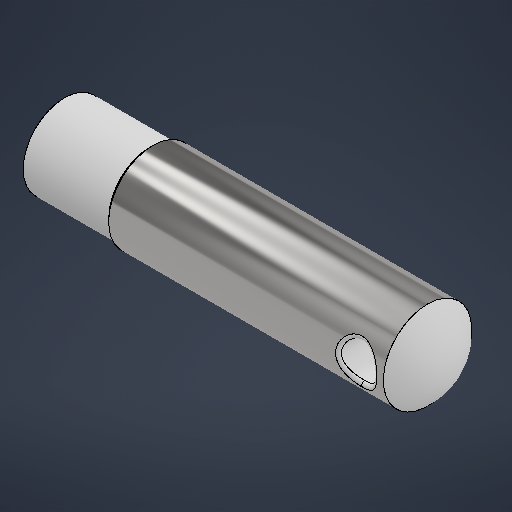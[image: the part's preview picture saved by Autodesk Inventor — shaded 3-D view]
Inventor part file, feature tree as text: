
AUTODESK INVENTOR PART (.ipt)
format: ipt  version: 2025.3 (Build 293356000, 356)  size: 287,232 bytes
history: native  units: mm
features: sketch x1, revolve x1, extrude x1, fillet x1, other x1
ambient origin geometry x8: Origin, YZ Plane, XZ Plane, XY Plane, X Axis, Y Axis, Z Axis, Center Point
bodies: Solid1 (feature_tree)
feature tree (5):
  sketch  "Sketch1"  dims[d0=10.2mm d3=15.0mm d6=50.0mm d8=15.0mm d9=10.0mm d10=6.0mm d11=360.0deg d12=65.0mm d13=0.5mm d14=0.5mm d15=57.0mm d16=0.0mm d17=0.0mm d18=0.5mm d19=14.0mm d20=60.0deg d21=3.385622mm]
  revolve  "Revolution1"  [1 undecoded]
  extrude  "Extrusion1"  Depth=50.0mm
  fillet  "Fillet1"  Radius=15.0mm
  other  "Finish1"
note: 1 required parameter value undecoded (feature->parameter linkage not recoverable at this tier; creation-order binding heuristic only, values carry confidence <= 0.55)
